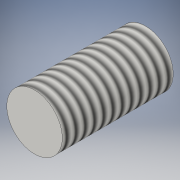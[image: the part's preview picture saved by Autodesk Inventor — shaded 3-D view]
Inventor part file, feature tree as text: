
AUTODESK INVENTOR PART (.ipt)
format: ipt  version: 2016 (Build 200138000, 138)  size: 118,784 bytes
history: native  units: in
note: dims shown in document units (in); Inventor stores cm internally (conversion verified against a paired STEP export)
features: extrude x1, thread x1, sketch x1
ambient origin geometry x8: Origin, YZ Plane, XZ Plane, XY Plane, X Axis, Y Axis, Z Axis, Center Point
bodies: Solid1 (feature_tree)
feature tree (3):
  extrude  "Extrusion1"  Depth=0.2362in TaperAngle=0.0deg
  thread  "Thread1"  [1 undecoded]
  sketch  "Sketch1"  dims[d0=0.1181in d1=0.2362in d2=0.0in d3=1.0in d4=0.0in]
note: 1 required parameter value undecoded (feature->parameter linkage not recoverable at this tier; creation-order binding heuristic only, values carry confidence <= 0.55)
